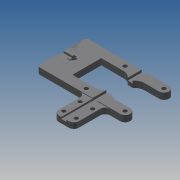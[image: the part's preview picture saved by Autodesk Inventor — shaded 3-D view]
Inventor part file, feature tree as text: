
AUTODESK INVENTOR PART (.ipt)
format: ipt  version: 2015 SP1 (Build 190203100, 203)  size: 433,152 bytes
history: native  units: mm
features: projected_geometry x20, sketch x10, extrude x10, fillet x4, plane x1
ambient origin geometry x8: Origin, YZ Plane, XZ Plane, XY Plane, X Axis, Y Axis, Z Axis, Center Point
bodies: Body1 (feature_tree)
feature tree (45):
  sketch  "Skizze1"  dims[d0=3.1mm d1=15.5mm]
  plane  "Arbeitsebene1"
  extrude  "Extrusion5"  Depth=3.1mm
  extrude  "Extrusion8"  Depth=22.0mm
  extrude  "Extrusion9"  Depth=11.0mm
  extrude  "Extrusion10"  Depth=8.0mm
  fillet  "Rundung1"  Radius=15.0mm
  fillet  "Rundung2"  Radius=40.0mm
  extrude  "Extrusion13"  Depth=8.0mm
  extrude  "Extrusion14"  Depth=15.0mm
  extrude  "Extrusion15"  Depth=3.0mm
  extrude  "Extrusion16"  Depth=2.4mm
  extrude  "Extrusion17"  Depth=7.0mm
  extrude  "Extrusion18"  Depth=4.0mm
  fillet  "Rundung3"  Radius=2.4mm
  fillet  "Rundung4"  Radius=1.9mm
  sketch  "Skizze4"  dims[d2=15.5mm d3=22.0mm]
  projected_geometry  "Projizierte Kontur2"
  sketch  "Skizze5"  dims[d4=16.5mm d5=11.0mm]
  projected_geometry  "Projizierte Kontur3"
  projected_geometry  "Projizierte Kontur4"
  projected_geometry  "Projizierte Kontur5"
  sketch  "Skizze6"  dims[d6=8.0mm d7=15.0mm d10=15.0mm d11=40.0mm]
  projected_geometry  "Projizierte Kontur6"
  sketch  "Skizze11"  dims[d17=8.0mm d19=8.0mm]
  projected_geometry  "Projizierte Kontur26"
  projected_geometry  "Projizierte Kontur27"
  projected_geometry  "Projizierte Kontur28"
  projected_geometry  "Projizierte Kontur29"
  projected_geometry  "Projizierte Kontur30"
  projected_geometry  "Projizierte Kontur31"
  sketch  "Skizze12"  dims[d22=35.0mm d23=15.0mm]
  projected_geometry  "Projizierte Kontur32"
  projected_geometry  "Projizierte Kontur33"
  sketch  "Skizze13"  dims[d28=5.0mm d29=0.0mm d34=3.0mm]
  projected_geometry  "Projizierte Kontur34"
  projected_geometry  "Projizierte Kontur35"
  projected_geometry  "Projizierte Kontur36"
  sketch  "Skizze16"  dims[d35=1.5mm d36=0.0mm d37=2.4mm]
  projected_geometry  "Projizierte Kontur51"
  sketch  "Skizze17"  dims[d38=5.5mm d39=7.0mm]
  projected_geometry  "Projizierte Kontur52"
  projected_geometry  "Projizierte Kontur53"
  sketch  "Skizze18"  dims[d40=3.2mm d41=0.0mm d42=4.0mm d43=2.4mm d44=1.9mm d45=0.0mm d46=2.0mm d47=2.0mm d61=3.0mm d62=4.0mm d63=8.0mm d64=8.0mm d65=6.0mm d66=6.0mm d67=5.0mm d68=0.0mm d69=1.9mm d70=0.0mm d71=9.0mm d72=1.5mm d73=0.0mm d75=6.0mm d76=25.0mm d77=0.0mm d78=3.0mm d79=3.0mm d80=3.0mm d81=3.0mm d82=18.0mm d84=3.0mm d85=3.0mm d86=5.0mm d87=5.0mm d88=0.0mm d89=0.5mm d90=25.0mm d91=0.0mm d92=4.0mm d93=4.0mm]
  projected_geometry  "Projizierte Kontur54"
